# Revit family: DIHT_Granular Pot Washer_900-TR--
name_source: partatom
category: Specialty Equipment
revit_build: Autodesk Revit 2016 (Build: 20161004_0715(x64)
units: mm (PartAtom-declared; Revit-internal decimal feet)

## family parameters
Always vertical = Yes
Cut with Voids When Loaded = No
OmniClass Number = 23.40.40.14.31
OmniClass Title = Cleaning and Disposal Equipment
Part Type = Normal
Room Calculation Point = No
Round Connector Dimension = Use Diameter
Shared = No
Work Plane-Based = No

## types (1)
- W1095 D910 H2100 mm PLUS
    Assembly Code = E1090320
    Basket Type = Ø735x240 mm
    Boiler Heating = 9 kW
    Boiler Temperature = 85
    Boiler capacity = 20.0 L
    Case_H = 1580 mm  [stored 5.18373 ft]
    Cold Water DN = 20 mm
    Cold Water DN Type = GAS
    Cold Water Flow = 0.0 L/s
    Depth = 910 mm
    Dishes Diameter = ---
    ELE_Frequency = 50 Hz
    ELE_Number of poles = 3
    ELE_Power = 13 kW
    ELE_Power Supply = 400 V
    Exhaust Pump Flow = 0.0 L/s
    Exhaust Pump Power = 0 W
    Exhaust Water DN = 32 mm
    File Release = R001
    Glass Max height = ---
    Height = 2100 mm
    Height Hood Open = 2100 mm
    IFC Classification = Dishwasher
    Keynote = GRANULES 900 TR PLUS
    LOD Data = 400
    LOD Model = 400
    Manufacturer = DIHR S.p.a.
    Mat Cabinet = ALI_Stainless Steel
    Mat Clearance = ALI_Clearance
    Mat Legs = ALI_Plastic_Black_Low Gloss
    Model = GRANULES 900 TR PLUS
    Noisiness = 79±0.7 dB(A)
    Product Code = DW110E
    Product Manufacturer = DIHR S.p.a.
    Product Series = GRANULES 900 TR PLUS
    Product URL = www.dihr.com/it/catalogo/lava-oggetti-a-granuli/granules
    Rinse Pump Flow = 2.5 L/s
    Rinse Pump Power = 250 W
    Tank Capacity = 103.0 L
    Tank Heating Element = 9000 kW
    Tank Temperature = 55
    Trays Type = 635 mm
    URL = https://www.dihr.com
    Volume = 2.09 m³
    Wash Pump Flow = 15.0 L/s
    Wash Pump Power = 3780 W
    Washing Cycles = Nr12_5/5    7/7    9/9    11/11    13/13    16/16 min
    Water Comsumption = 4.4 L
    Water Hardness = 2-8°F
    Water Pressure = 200-400 kPa
    Weight net = 320.00 kg
    Width = 1095 mm  [stored 3.59252 ft]

note: [stored X ft] marks values corroborated as IEEE doubles in the binary element streams (Revit-internal decimal feet)

## geometry (parser evidence)
native form markers: Sweep x10
no freeform markers — native parametric forms only
